# Revit family: Cortadora_CA-2V_GENERADO
name_source: partatom
category: Equipos especializados
units: mm (PartAtom-declared; Revit-internal decimal feet)

## family parameters
Compartido = No
Corte con vacíos al cargar = No
Cota de conector redondo = Diámetro de uso
Número OmniClass = 23.21.21.31.19.11
Punto de cálculo de habitación = No
Se basa en plano de trabajo = No
Siempre vertical = Sí
Tipo de pieza = Normal

## types (5) — shared parameters
Comentarios de tipo = Compact, variable speed vegetable slicer. "Brushless" technology: maximum efficiency.
Cycle = 50 Hz
Depth = 309 mm  [stored 1.01378 ft]
Fabricante = SAMMIC S.L.
Foodservice Equipment Identifier = Sí
Height = 533 mm  [stored 1.74869 ft]
Phase = 1
Revision Code = 1
Specification by Manufacturer = Compact ULTRA line. Variable speed motor block + vegetable slicer attachment.
URL = https://www.sammic.com
URL Cutsheet = http://www.sammic.com
Weight in Pounds = 28.4
Width = 378 mm  [stored 1.24016 ft]
zero-valued in all types: Elevación por defecto

## per-type parameters (varying)
| type | FL Amps | HP | Modelo | Volts | Watts |
| Vegetable preparation machine CA-2V 230/50-60/1 | 7 A | 1.48 | 1050962 | 230 V | 1100 W |
| Vegetable preparation machine CA-2V 230/50-60/1 AUS | 7 A | 1.48 | 1050964 | 230 V | 1100 W |
| Vegetable preparation machine CA-2V 230/50-60/1 UK | 7 A | 1.48 | 1050965 | 230 V | 1100 W |
| Vegetable preparation machine CA-2V 120/50-60/1 | 5 A | 2.01 | 1050970 | 120 V | 1500 W |
| Vegetable preparation machine CA-2V 2D 120/50-60/1 · 2 discs included | 5 A | 2.01 | 1050972 | 120 V | 1500 W |

note: column(s) folded — value = type name in every type: Descripción

note: [stored X ft] marks values corroborated as IEEE doubles in the binary element streams (Revit-internal decimal feet)
